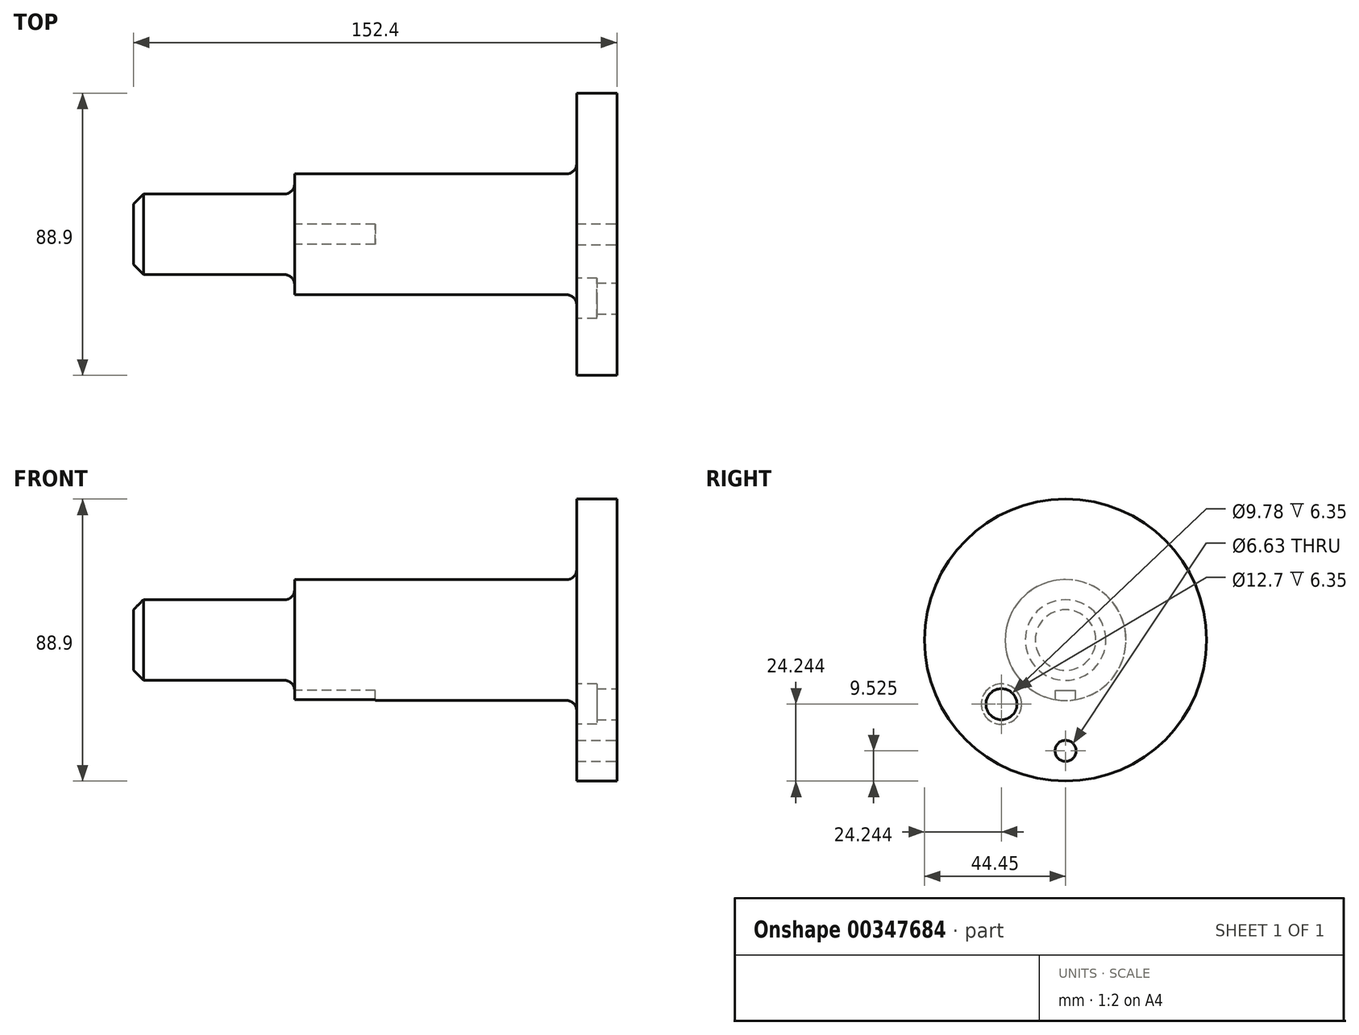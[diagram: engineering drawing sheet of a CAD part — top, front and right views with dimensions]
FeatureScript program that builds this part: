
annotation { "Feature Type Name" : "Feature", "Feature Type Description" : "" }
export const myFeature = defineFeature(function(context is Context, id is Id, definition is map)
    precondition{}
    {
        {
            var Q0;
            Q0=qCreatedBy(makeId("Front.planeOp"),FACE);
            var sketch = newSketch(context, id + "F0", { "sketchPlane" : qUnion([Q0])});
            skLineSegment(sketch, "E0", {"start": v(0, 0) * mm, "end": v(152.4, 0) * mm});
            skLineSegment(sketch, "E1", {"start": v(0, 0) * mm, "end": v(0, 12.7) * mm});
            skLineSegment(sketch, "E2", {"start": v(50.8, 12.7) * mm, "end": v(0, 12.7) * mm});
            skLineSegment(sketch, "E3", {"start": v(50.8, 12.7) * mm, "end": v(50.8, 19.05) * mm});
            skLineSegment(sketch, "E4", {"start": v(50.8, 19.05) * mm, "end": v(139.7, 19.05) * mm});
            skLineSegment(sketch, "E5", {"start": v(139.7, 19.05) * mm, "end": v(139.7, 44.45) * mm});
            skLineSegment(sketch, "E6", {"start": v(139.7, 44.45) * mm, "end": v(152.4, 44.45) * mm});
            skLineSegment(sketch, "E7", {"start": v(152.4, 44.45) * mm, "end": v(152.4, 0) * mm});
            skSolve(sketch);
        }
        {
            var Q0;
            Q0 = qSketchRegion(id + "F0", true);
            var Q1;
            Q1=sQuery(id+"F0.wireOp",EDGE,"E0");
            revolve(context, id + "F1", {"entities" : qUnion([Q0]), "axis" : qUnion([Q1]), "revolveType" : RevolveType.FULL});
        }
        {
            var Q0;
            Q0=makeQuery(id+"F1.opRevolve","SWEPT_EDGE",EDGE,{"disambiguationData":[OSD([sQuery(id+"F0.wireOp",EDGE,"E2"),sQuery(id+"F0.wireOp",EDGE,"E3")])]});
            fillet(context, id + "F2", {"entities" : qUnion([Q0]), "radius" : 3.17 * mm, "tangentPropagation" : true, "allowEdgeOverflow" : false});
        }
        {
            var Q0;
            Q0=makeQuery(id+"F1.opRevolve","SWEPT_EDGE",EDGE,{"disambiguationData":[OSD([sQuery(id+"F0.wireOp",EDGE,"E4"),sQuery(id+"F0.wireOp",EDGE,"E5")])]});
            fillet(context, id + "F3", {"entities" : qUnion([Q0]), "radius" : 3.17 * mm, "tangentPropagation" : true, "allowEdgeOverflow" : false});
        }
        {
            var Q0;
            Q0=makeQuery(id+"F1.opRevolve","SWEPT_EDGE",EDGE,{"disambiguationData":[OSD([sQuery(id+"F0.wireOp",EDGE,"E1"),sQuery(id+"F0.wireOp",EDGE,"E2")])]});
            chamfer(context, id + "F4", {"entities" : qUnion([Q0]), "width" : 3.17 * mm, "tangentPropagation" : true});
        }
        {
            var Q0;
            Q0=makeQuery(id+"F1.opRevolve","SWEPT_FACE",FACE,{"disambiguationData":[OSD([sQuery(id+"F0.wireOp",EDGE,"E7")])]});
            var sketch = newSketch(context, id + "F5", { "sketchPlane" : qUnion([Q0])});
            skCircle(sketch, "E8", {"center": v(0, -34.93) * mm, "radius": 3.31 * mm});
            skLineSegment(sketch, "E9", {"start": v(0, -34.93) * mm, "end": v(0, 0) * mm, "construction": true});
            skSolve(sketch);
        }
        {
            var Q0;
            Q0 = qSketchRegion(id + "F5", true);
            extrude(context, id + "F6", {"entities" : qUnion([Q0]), "operationType" : NewBodyOperationType.REMOVE, "endBound" : BoundingType.THROUGH_ALL, "oppositeDirection" : true, "depth" : 25.4 * mm});
        }
        {
            var Q0;
            Q0=makeQuery(id+"F1.opRevolve","SWEPT_FACE",FACE,{"disambiguationData":[OSD([sQuery(id+"F0.wireOp",EDGE,"E3")])]});
            var sketch = newSketch(context, id + "F7", { "sketchPlane" : qUnion([Q0])});
            skLineSegment(sketch, "E10", {"start": v(0, 0) * mm, "end": v(0, -19.05) * mm});
            skLineSegment(sketch, "E11.bottom", {"start": v(3.17, -19.05) * mm, "end": v(-3.17, -19.05) * mm});
            skLineSegment(sketch, "E11.left", {"start": v(3.17, -19.05) * mm, "end": v(3.17, -15.87) * mm});
            skLineSegment(sketch, "E11.right", {"start": v(-3.17, -19.05) * mm, "end": v(-3.17, -15.87) * mm});
            skLineSegment(sketch, "E12", {"start": v(3.18, -15.87) * mm, "end": v(-3.18, -15.87) * mm});
            skSolve(sketch);
        }
        {
            var Q0;
            Q0 = qSketchRegion(id + "F7", true);
            extrude(context, id + "F8", {"entities" : qUnion([Q0]), "operationType" : NewBodyOperationType.REMOVE, "oppositeDirection" : true, "depth" : 25.4 * mm});
        }
        {
            var Q0;
            Q0=makeQuery(id+"F1.opRevolve","SWEPT_FACE",FACE,{"disambiguationData":[OSD([sQuery(id+"F0.wireOp",EDGE,"E7")])]});
            var sketch = newSketch(context, id + "F9", { "sketchPlane" : qUnion([Q0])});
            skPoint(sketch, "E13.middle", {"position": v(0, 0) * mm});
            skCircle(sketch, "E14", {"center": v(-20.2, -20.2) * mm, "radius": 4.89 * mm});
            skLineSegment(sketch, "E15", {"start": v(0, 0) * mm, "end": v(-20.2, -20.2) * mm, "construction": true});
            skLineSegment(sketch, "E16", {"start": v(0, 0) * mm, "end": v(-44.45, 0) * mm, "construction": true});
            skSolve(sketch);
        }
        {
            var Q0;
            Q0 = qSketchRegion(id + "F9", true);
            extrude(context, id + "F10", {"entities" : qUnion([Q0]), "operationType" : NewBodyOperationType.REMOVE, "endBound" : BoundingType.THROUGH_ALL, "oppositeDirection" : true, "depth" : 25.4 * mm});
        }
        {
            var Q0;
            Q0=makeQuery(id+"F1.opRevolve","SWEPT_FACE",FACE,{"disambiguationData":[OSD([sQuery(id+"F0.wireOp",EDGE,"E5")])]});
            var sketch = newSketch(context, id + "F11", { "sketchPlane" : qUnion([Q0])});
            skCircle(sketch, "E17", {"center": v(20.2, -20.2) * mm, "radius": 6.35 * mm});
            skSolve(sketch);
        }
        {
            var Q0;
            Q0 = qSketchRegion(id + "F11", true);
            extrude(context, id + "F12", {"entities" : qUnion([Q0]), "operationType" : NewBodyOperationType.REMOVE, "oppositeDirection" : true, "depth" : 6.35 * mm});
        }
    });
